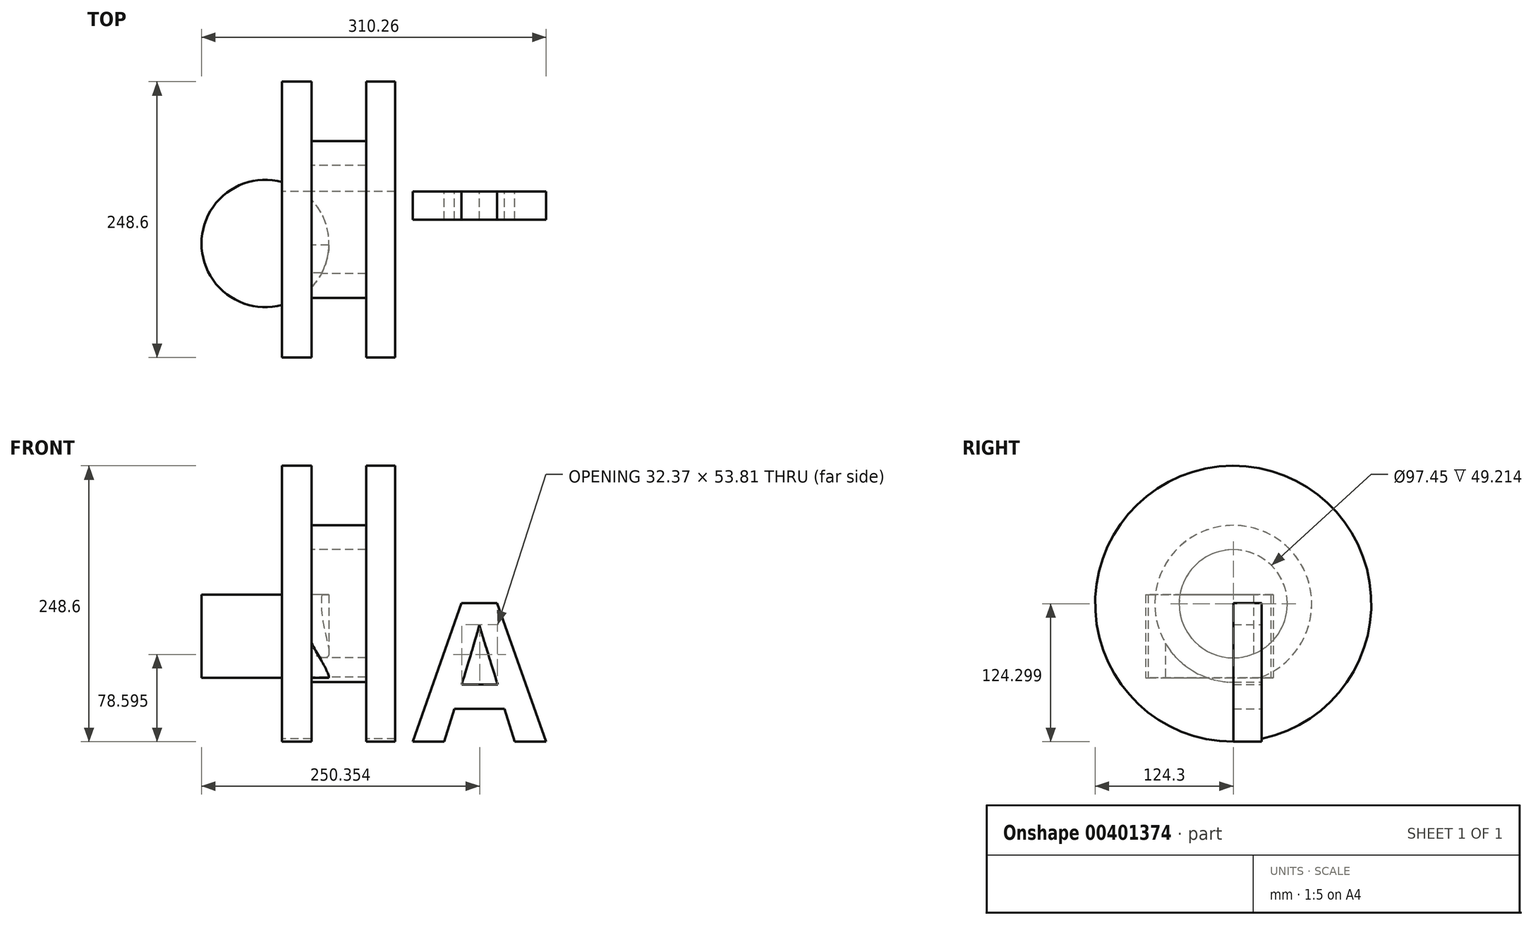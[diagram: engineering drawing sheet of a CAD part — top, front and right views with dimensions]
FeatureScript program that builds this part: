
annotation { "Feature Type Name" : "Feature", "Feature Type Description" : "" }
export const myFeature = defineFeature(function(context is Context, id is Id, definition is map)
    precondition{}
    {
        {
            var Q0;
            Q0=qCreatedBy(makeId("Front.planeOp"),FACE);
            var sketch = newSketch(context, id + "F0", { "sketchPlane" : qUnion([Q0])});
            skText(sketch, "E0", { "text": "HA", "fontName": "OpenSans-Bold.ttf"});
            const initialGuessF0  = {"E0": [-0.1012, -0.05744, 1, 0, 0.12536]};
            skSetInitialGuess(sketch, initialGuessF0);
            skSolve(sketch);
        }
        {
            var Q0;
            Q0 = qSketchRegion(id + "F0", true);
            extrude(context, id + "F1", {"entities" : qUnion([Q0]), "depth" : 25.4 * mm});
        }
        {
            var Q0;
            Q0=qCreatedBy(makeId("Top.planeOp"),FACE);
            var sketch = newSketch(context, id + "F2", { "sketchPlane" : qUnion([Q0])});
            skCircle(sketch, "E1", {"center": v(-100.72, -46.88) * mm, "radius": 57.38 * mm});
            skSolve(sketch);
        }
        {
            var Q0;
            Q0=makeQuery(id+"F1.opExtrude","CAP_FACE",FACE,{"disambiguationData":[OSD([sQuery(id+"F0.wireOp",EDGE,"E0.sketch_text.stroke-0"),sQuery(id+"F0.wireOp",EDGE,"E0.sketch_text.stroke-1"),sQuery(id+"F0.wireOp",EDGE,"E0.sketch_text.stroke-2"),sQuery(id+"F0.wireOp",EDGE,"E0.sketch_text.stroke-3"),sQuery(id+"F0.wireOp",EDGE,"E0.sketch_text.stroke-4"),sQuery(id+"F0.wireOp",EDGE,"E0.sketch_text.stroke-5"),sQuery(id+"F0.wireOp",EDGE,"E0.sketch_text.stroke-6"),sQuery(id+"F0.wireOp",EDGE,"E0.sketch_text.stroke-7"),sQuery(id+"F0.wireOp",EDGE,"E0.sketch_text.stroke-8"),sQuery(id+"F0.wireOp",EDGE,"E0.sketch_text.stroke-9"),sQuery(id+"F0.wireOp",EDGE,"E0.sketch_text.stroke-10"),sQuery(id+"F0.wireOp",EDGE,"E0.sketch_text.stroke-11")])],"isStart":false});
            var Q1;
            Q1=makeQuery(id+"F1.opExtrude","CAP_EDGE",EDGE,{"disambiguationData":[OSD([sQuery(id+"F0.wireOp",EDGE,"E0.sketch_text.stroke-6")])],"isStart":false});
            revolve(context, id + "F3", {"operationType" : NewBodyOperationType.ADD, "entities" : qUnion([Q0]), "axis" : qUnion([Q1]), "revolveType" : RevolveType.FULL});
        }
        {
            var Q0;
            Q0=makeQuery(id+"F2.imprint","IMPRINT",FACE,{"disambiguationData":[TD([[makeQuery(id+"F2.imprint","IMPRINT",EDGE,{"derivedFrom":sQuery(id+"F2.wireOp",EDGE,"E1")}),1.0]])]});
            extrude(context, id + "F4", {"entities" : qUnion([Q0]), "operationType" : NewBodyOperationType.ADD, "depth" : 74.93 * mm});
        }
    });
